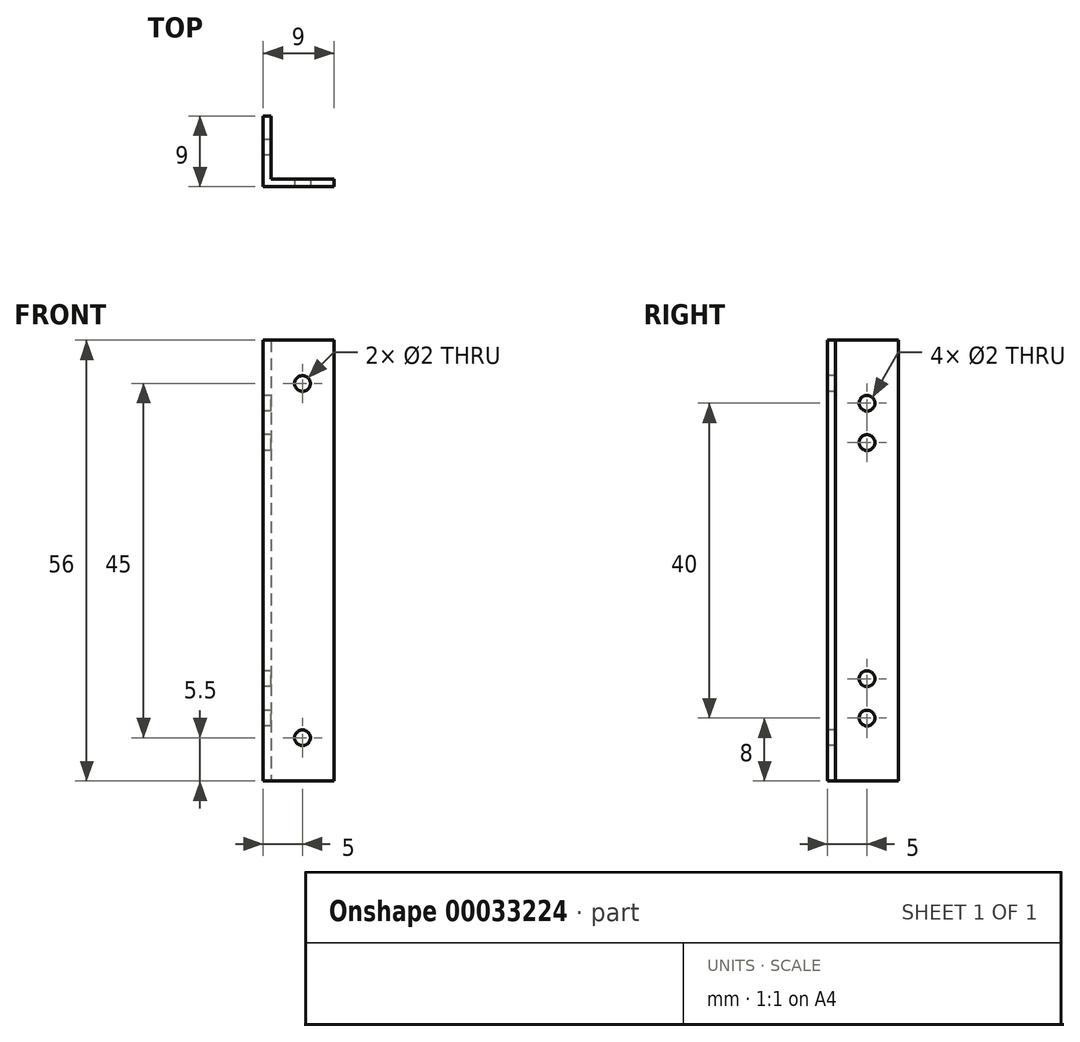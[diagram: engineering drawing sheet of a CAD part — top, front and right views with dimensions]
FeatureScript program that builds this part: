
annotation { "Feature Type Name" : "Feature", "Feature Type Description" : "" }
export const myFeature = defineFeature(function(context is Context, id is Id, definition is map)
    precondition{}
    {
        {
            var Q0;
            Q0=qCreatedBy(makeId("Top.planeOp"),FACE);
            var sketch = newSketch(context, id + "F0", { "sketchPlane" : qUnion([Q0])});
            skLineSegment(sketch, "E0.bottom", {"start": v(0, 0) * mm, "end": v(9, 0) * mm});
            skLineSegment(sketch, "E0.top", {"start": v(0, 9) * mm, "end": v(1, 9) * mm});
            skLineSegment(sketch, "E0.left", {"start": v(0, 0) * mm, "end": v(0, 9) * mm});
            skLineSegment(sketch, "E0.right", {"start": v(9, 0) * mm, "end": v(9, 1) * mm});
            skLineSegment(sketch, "E1.top", {"start": v(9, 1) * mm, "end": v(1, 1) * mm});
            skLineSegment(sketch, "E1.right", {"start": v(1, 9) * mm, "end": v(1, 1) * mm});
            skSolve(sketch);
        }
        {
            var Q0;
            Q0=qSketchRegion(id+"F0",true);
            extrude(context, id + "F1", {"entities" : qUnion([Q0]), "depth" : 56 * mm});
        }
        {
            var Q0;
            Q0=makeQuery(id+"F1.opExtrude","SWEPT_FACE",FACE,{"disambiguationData":[OSD([sQuery(id+"F0.wireOp",EDGE,"E0.bottom")])]});
            var sketch = newSketch(context, id + "F2", { "sketchPlane" : qUnion([Q0])});
            skLineSegment(sketch, "E2", {"start": v(0, 28) * mm, "end": v(9, 28) * mm, "construction": true});
            skCircle(sketch, "E3", {"center": v(5, 50.5) * mm, "radius": 1 * mm});
            skCircle(sketch, "E4.MirrorC", {"center": v(5, 5.5) * mm, "radius": 1 * mm});
            skSolve(sketch);
        }
        {
            var Q0;
            Q0=qSketchRegion(id+"F2",true);
            extrude(context, id + "F3", {"entities" : qUnion([Q0]), "operationType" : NewBodyOperationType.REMOVE, "endBound" : BoundingType.UP_TO_NEXT, "oppositeDirection" : true, "depth" : 25 * mm});
        }
        {
            var Q0;
            Q0=makeQuery(id+"F1.opExtrude","SWEPT_FACE",FACE,{"disambiguationData":[OSD([sQuery(id+"F0.wireOp",EDGE,"E0.left")])]});
            var sketch = newSketch(context, id + "F4", { "sketchPlane" : qUnion([Q0])});
            skLineSegment(sketch, "E5", {"start": v(-9, 28) * mm, "end": v(0, 28) * mm, "construction": true});
            skCircle(sketch, "E6", {"center": v(-5, 48) * mm, "radius": 1 * mm});
            skCircle(sketch, "E7.MirrorC", {"center": v(-5, 8) * mm, "radius": 1 * mm});
            skCircle(sketch, "E8", {"center": v(-5, 13) * mm, "radius": 1 * mm});
            skCircle(sketch, "E9.MirrorC", {"center": v(-5, 43) * mm, "radius": 1 * mm});
            skSolve(sketch);
        }
        {
            var Q0;
            Q0=qSketchRegion(id+"F4",true);
            extrude(context, id + "F5", {"entities" : qUnion([Q0]), "operationType" : NewBodyOperationType.REMOVE, "endBound" : BoundingType.UP_TO_NEXT, "oppositeDirection" : true, "depth" : 25 * mm});
        }
    });
